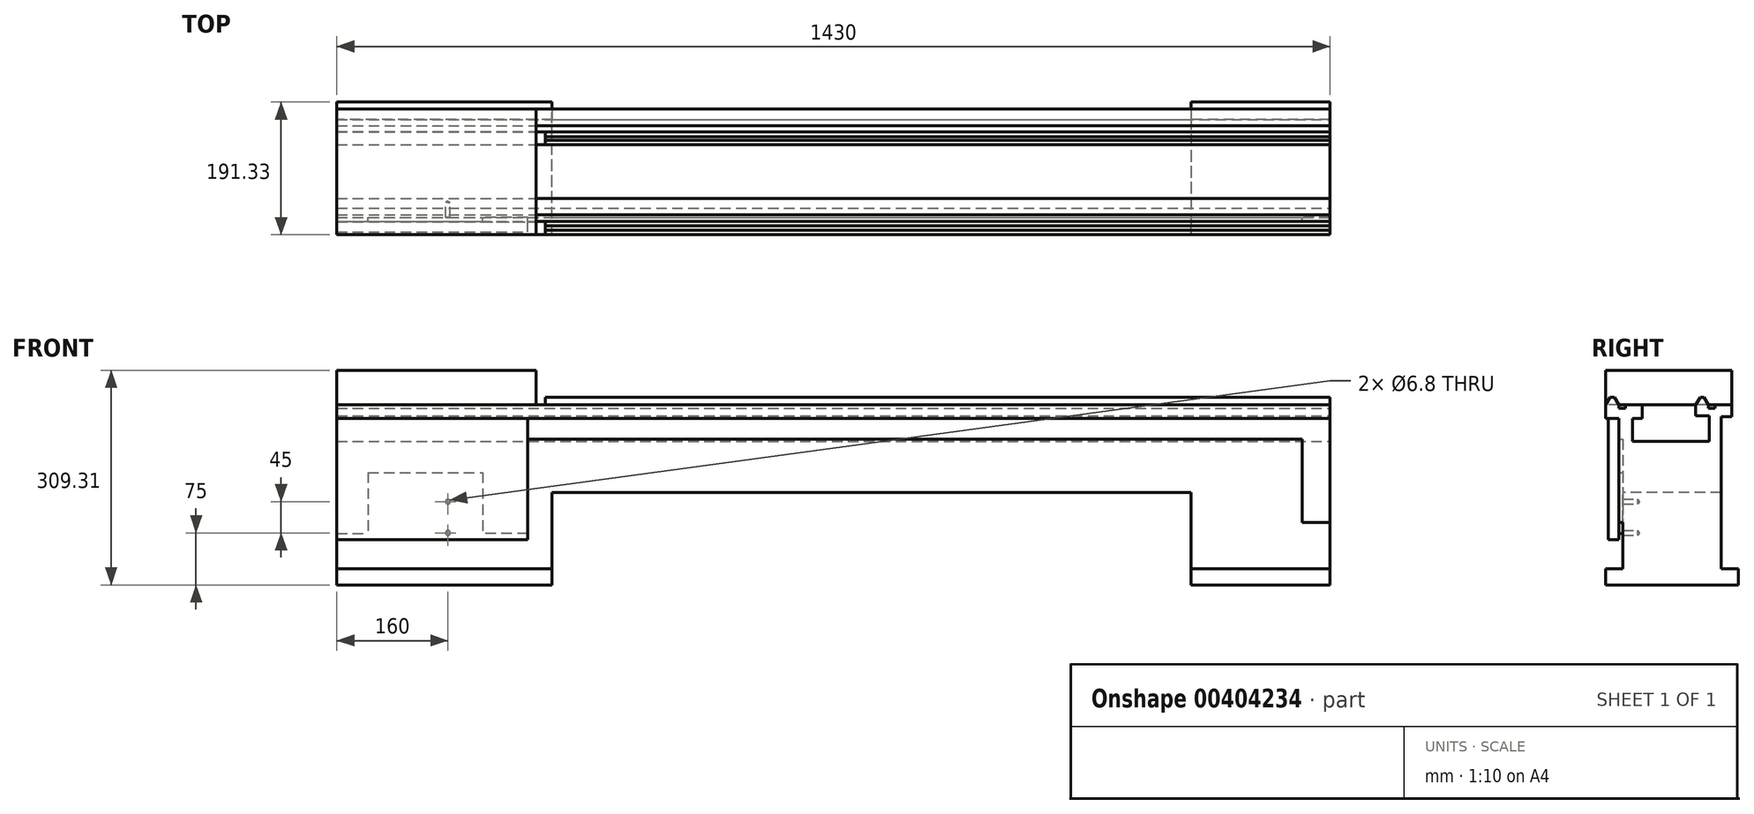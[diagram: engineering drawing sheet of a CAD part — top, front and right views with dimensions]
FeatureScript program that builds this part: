
annotation { "Feature Type Name" : "Feature", "Feature Type Description" : "" }
export const myFeature = defineFeature(function(context is Context, id is Id, definition is map)
    precondition{}
    {
        {
            var Q0;
            Q0=qCreatedBy(makeId("Right.planeOp"),FACE);
            var sketch = newSketch(context, id + "F0", { "sketchPlane" : qUnion([Q0])});
            skLineSegment(sketch, "E0", {"start": v(0, 19.31) * mm, "end": v(3.83, 25.95) * mm});
            skLineSegment(sketch, "E1", {"start": v(15.2, 25.95) * mm, "end": v(19.04, 19.31) * mm});
            skLineSegment(sketch, "E2", {"start": v(0, 19.31) * mm, "end": v(19.04, 19.31) * mm, "construction": true});
            skPoint(sketch, "E3.start.orphan", {"position": v(0, 0) * mm});
            skLineSegment(sketch, "E4", {"start": v(0, 0) * mm, "end": v(0, 19.31) * mm});
            skLineSegment(sketch, "E5", {"start": v(9.52, 25.95) * mm, "end": v(9.52, 19.31) * mm, "construction": true});
            skLineSegment(sketch, "E6", {"start": v(28.45, 19.31) * mm, "end": v(28.45, 14.51) * mm});
            skLineSegment(sketch, "E7", {"start": v(52.4, 19.31) * mm, "end": v(52.4, 0) * mm});
            skLineSegment(sketch, "E8", {"start": v(19.04, 19.31) * mm, "end": v(19.04, 14.51) * mm});
            skLineSegment(sketch, "E9", {"start": v(19.04, 14.51) * mm, "end": v(28.45, 14.51) * mm});
            skLineSegment(sketch, "E10", {"start": v(0, 0) * mm, "end": v(18.78, 0) * mm});
            skLineSegment(sketch, "E11", {"start": v(38.3, -32.97) * mm, "end": v(38.3, -32.97) * mm});
            skLineSegment(sketch, "E12", {"start": v(38.3, -32.97) * mm, "end": v(148.72, -32.97) * mm});
            skLineSegment(sketch, "E13", {"start": v(129.6, 19.31) * mm, "end": v(129.6, 3.67) * mm});
            skLineSegment(sketch, "E14.trimOffspring", {"start": v(28.45, 19.31) * mm, "end": v(52.4, 19.31) * mm});
            skLineSegment(sketch, "E15", {"start": v(136.07, 30.53) * mm, "end": v(141.32, 30.53) * mm});
            skLineSegment(sketch, "E16", {"start": v(129.6, 19.31) * mm, "end": v(136.07, 30.53) * mm});
            skLineSegment(sketch, "E17", {"start": v(141.32, 30.53) * mm, "end": v(147.8, 19.31) * mm});
            skLineSegment(sketch, "E18", {"start": v(181.37, 19.31) * mm, "end": v(181.37, 2.05) * mm});
            skLineSegment(sketch, "E19", {"start": v(147.8, 19.31) * mm, "end": v(147.8, 14.51) * mm});
            skLineSegment(sketch, "E20", {"start": v(147.8, 14.51) * mm, "end": v(157.11, 14.51) * mm});
            skLineSegment(sketch, "E21", {"start": v(157.11, 14.51) * mm, "end": v(157.11, 19.31) * mm});
            skLineSegment(sketch, "E22.trimOffspring", {"start": v(129.6, 19.31) * mm, "end": v(147.8, 19.31) * mm, "construction": true});
            skLineSegment(sketch, "E23", {"start": v(52.4, 0) * mm, "end": v(38.3, 0) * mm});
            skLineSegment(sketch, "E24", {"start": v(148.72, -32.97) * mm, "end": v(148.72, 3.67) * mm});
            skLineSegment(sketch, "E25", {"start": v(38.3, 0) * mm, "end": v(38.3, -32.97) * mm});
            skLineSegment(sketch, "E26", {"start": v(157.11, 19.31) * mm, "end": v(181.37, 19.31) * mm});
            skLineSegment(sketch, "E27", {"start": v(24.78, -106.67) * mm, "end": v(166.11, -106.67) * mm});
            skLineSegment(sketch, "E28", {"start": v(181.37, 2.05) * mm, "end": v(166.11, 2.05) * mm});
            skLineSegment(sketch, "E29", {"start": v(166.11, 2.05) * mm, "end": v(166.11, -106.67) * mm});
            skLineSegment(sketch, "E30", {"start": v(129.6, 3.67) * mm, "end": v(148.72, 3.67) * mm});
            skLineSegment(sketch, "E31", {"start": v(138.7, 30.53) * mm, "end": v(-64.68, 30.53) * mm, "construction": true});
            skLineSegment(sketch, "E32", {"start": v(3.83, 25.95) * mm, "end": v(6.48, 30.53) * mm});
            skLineSegment(sketch, "E33", {"start": v(15.2, 25.95) * mm, "end": v(12.56, 30.53) * mm});
            skLineSegment(sketch, "E34", {"start": v(12.56, 30.53) * mm, "end": v(6.48, 30.53) * mm});
            skLineSegment(sketch, "E35", {"start": v(24.78, -30) * mm, "end": v(24.78, -106.67) * mm});
            skLineSegment(sketch, "E36", {"start": v(24.78, -30) * mm, "end": v(18.78, -30) * mm});
            skLineSegment(sketch, "E37", {"start": v(18.78, -30) * mm, "end": v(18.78, 0) * mm});
            skSolve(sketch);
        }
        {
            var Q0;
            Q0=makeQuery(id+"F0.imprint","IMPRINT",FACE,{"disambiguationData":[TD([[makeQuery(id+"F0.imprint","IMPRINT",EDGE,{"derivedFrom":sQuery(id+"F0.wireOp",EDGE,"E0")}),-1.0]])]});
            extrude(context, id + "F1", {"entities" : qUnion([Q0]), "oppositeDirection" : true, "depth" : 1430 * mm, "offsetDistance" : 25 * mm});
        }
        {
            var Q0;
            Q0=makeQuery(id+"F1.opExtrude","SWEPT_FACE",FACE,{"disambiguationData":[OSD([sQuery(id+"F0.wireOp",EDGE,"E27")])]});
            var sketch = newSketch(context, id + "F2", { "sketchPlane" : qUnion([Q0])});
            skLineSegment(sketch, "E38.bottom", {"start": v(-1430, -24.78) * mm, "end": v(-1120, -24.78) * mm});
            skLineSegment(sketch, "E38.top", {"start": v(-1430, -166.11) * mm, "end": v(-1120, -166.11) * mm});
            skLineSegment(sketch, "E38.left", {"start": v(-1430, -24.78) * mm, "end": v(-1430, -166.11) * mm});
            skLineSegment(sketch, "E38.right", {"start": v(-1120, -24.78) * mm, "end": v(-1120, -166.11) * mm});
            skSolve(sketch);
        }
        {
            var Q0;
            Q0=makeQuery(id+"F2.imprint","IMPRINT",FACE,{"disambiguationData":[TD([[makeQuery(id+"F2.imprint","IMPRINT",EDGE,{"derivedFrom":sQuery(id+"F2.wireOp",EDGE,"E38.bottom")}),-1.0]])]});
            extrude(context, id + "F3", {"entities" : qUnion([Q0]), "operationType" : NewBodyOperationType.ADD, "depth" : 133.33 * mm, "offsetDistance" : 25 * mm});
        }
        {
            var Q0;
            Q0=makeQuery(id+"F1.opExtrude","SWEPT_FACE",FACE,{"disambiguationData":[OSD([sQuery(id+"F0.wireOp",EDGE,"E27")])]});
            var sketch = newSketch(context, id + "F4", { "sketchPlane" : qUnion([Q0])});
            skLineSegment(sketch, "E39.bottom", {"start": v(0, -166.11) * mm, "end": v(-200, -166.11) * mm});
            skLineSegment(sketch, "E39.top", {"start": v(0, -24.78) * mm, "end": v(-200, -24.78) * mm});
            skLineSegment(sketch, "E39.left", {"start": v(0, -166.11) * mm, "end": v(0, -24.78) * mm});
            skLineSegment(sketch, "E39.right", {"start": v(-200, -166.11) * mm, "end": v(-200, -24.78) * mm});
            skSolve(sketch);
        }
        {
            var Q0;
            Q0=makeQuery(id+"F4.imprint","IMPRINT",FACE,{"disambiguationData":[TD([[makeQuery(id+"F4.imprint","IMPRINT",EDGE,{"derivedFrom":sQuery(id+"F4.wireOp",EDGE,"E39.bottom")}),1.0]])]});
            extrude(context, id + "F5", {"entities" : qUnion([Q0]), "operationType" : NewBodyOperationType.ADD, "depth" : 133.33 * mm, "offsetDistance" : 25 * mm});
        }
        {
            var Q0;
            Q0=makeQuery(id+"F5.boolean.opBoolean","MERGE",FACE,{"derivedFrom":[makeQuery(id+"F3.boolean.opBoolean","MERGE",FACE,{"derivedFrom":[makeQuery(id+"F1.opExtrude","SWEPT_FACE",FACE,{"disambiguationData":[OSD([sQuery(id+"F0.wireOp",EDGE,"E35")])]}),makeQuery(id+"F3.opExtrude","SWEPT_FACE",FACE,{"disambiguationData":[OSD([sQuery(id+"F2.wireOp",EDGE,"E38.bottom")])]})]}),makeQuery(id+"F5.opExtrude","SWEPT_FACE",FACE,{"disambiguationData":[OSD([sQuery(id+"F4.wireOp",EDGE,"E39.top")])]})]});
            var sketch = newSketch(context, id + "F6", { "sketchPlane" : qUnion([Q0])});
            skLineSegment(sketch, "E40", {"start": v(-1270, -115.03) * mm, "end": v(-1270, -199.05) * mm, "construction": true});
            skLineSegment(sketch, "E41", {"start": v(-1270, -199.05) * mm, "end": v(-1270, -115.03) * mm, "construction": true});
            skPoint(sketch, "E42", {"position": v(-1270, -120) * mm});
            skPoint(sketch, "E43", {"position": v(-1270, -165) * mm});
            skSolve(sketch);
        }
        {
            var Q0;
            Q0=sQuery(id+"F6.wireOp",VERTEX,"E42");
            var Q1;
            Q1=sQuery(id+"F6.wireOp",VERTEX,"E43");
            var Q2;
            Q2=makeQuery(id+"F1.opExtrude","SWEPT_BODY",BODY,{"disambiguationData":[OSD([sQuery(id+"F0.wireOp",EDGE,"E0"),sQuery(id+"F0.wireOp",EDGE,"E1"),sQuery(id+"F0.wireOp",EDGE,"E4"),sQuery(id+"F0.wireOp",EDGE,"E6"),sQuery(id+"F0.wireOp",EDGE,"E7"),sQuery(id+"F0.wireOp",EDGE,"E8"),sQuery(id+"F0.wireOp",EDGE,"E9"),sQuery(id+"F0.wireOp",EDGE,"E10"),sQuery(id+"F0.wireOp",EDGE,"YCXMaznk-yFnF-7irV-mpq2-gFufozlePJW7"),sQuery(id+"F0.wireOp",EDGE,"E12"),sQuery(id+"F0.wireOp",EDGE,"E13"),sQuery(id+"F0.wireOp",EDGE,"E14.trimOffspring"),sQuery(id+"F0.wireOp",EDGE,"E15"),sQuery(id+"F0.wireOp",EDGE,"E16"),sQuery(id+"F0.wireOp",EDGE,"E17"),sQuery(id+"F0.wireOp",EDGE,"E18"),sQuery(id+"F0.wireOp",EDGE,"E19"),sQuery(id+"F0.wireOp",EDGE,"E20"),sQuery(id+"F0.wireOp",EDGE,"E21"),sQuery(id+"F0.wireOp",EDGE,"E23"),sQuery(id+"F0.wireOp",EDGE,"E24"),sQuery(id+"F0.wireOp",EDGE,"E25"),sQuery(id+"F0.wireOp",EDGE,"E26"),sQuery(id+"F0.wireOp",EDGE,"E27"),sQuery(id+"F0.wireOp",EDGE,"E28"),sQuery(id+"F0.wireOp",EDGE,"E29"),sQuery(id+"F0.wireOp",EDGE,"E30"),sQuery(id+"F0.wireOp",EDGE,"E32"),sQuery(id+"F0.wireOp",EDGE,"E33"),sQuery(id+"F0.wireOp",EDGE,"E34"),sQuery(id+"F0.wireOp",EDGE,"nFRyOStG-R2Nf-dePJ-d9Yt-8JFO99bLOjxj"),sQuery(id+"F0.wireOp",EDGE,"E35")])]});
            hole(context, id + "F7", {"style" : HoleStyle.SIMPLE, "endStyle" : HoleEndStyle.BLIND, "standardTappedOrClearance" : lookupTablePath({ "standard" : "ISO", "engagement" : "75%", "pitch" : "1.25 mm", "size" : "M8", "type" : "Tapped" }), "standardBlindInLast" : lookupTablePath({ "standard" : "ISO", "engagement" : "75%", "pitch" : "1.25 mm", "size" : "M8", "type" : "Tapped" }), "holeDiameter" : 6.8 * mm, "majorDiameter" : 8 * mm, "showTappedDepth" : true, "holeDepth" : 21.65 * mm, "isTappedThrough" : true, "tappedDepth" : 17.9 * mm, "tapClearance" : 3, "startFromSketch" : true, "locations" : qUnion([Q0, Q1]), "scope" : qUnion([Q2])});
        }
        {
            var Q0;
            {var subQ0=sQuery(id+"F2.wireOp",EDGE,"E38.bottom");Q0=makeQuery(id+"F6.imprint","IMPRINT",FACE,{"disambiguationData":[TD([[makeQuery(id+"F6.imprint","IMPRINT",EDGE,{"derivedFrom":makeQuery(id+"F3.opExtrude","CAP_EDGE",EDGE,{"disambiguationData":[OSD([subQ0])],"isStart":false})}),1.0]])]});}
            var sketch = newSketch(context, id + "F8", { "sketchPlane" : qUnion([Q0])});
            skLineSegment(sketch, "E44.bottom", {"start": v(-1430, -30) * mm, "end": v(-1155, -30) * mm});
            skLineSegment(sketch, "E44.top", {"start": v(-1385, -78) * mm, "end": v(-1220, -78) * mm});
            skLineSegment(sketch, "E45.top", {"start": v(-1430, -166) * mm, "end": v(-1385, -166) * mm});
            skLineSegment(sketch, "E45.right", {"start": v(-1385, -78) * mm, "end": v(-1385, -166) * mm});
            skLineSegment(sketch, "E46.top", {"start": v(-1155, -166) * mm, "end": v(-1220, -166) * mm});
            skLineSegment(sketch, "E46.right", {"start": v(-1220, -78) * mm, "end": v(-1220, -166) * mm});
            skLineSegment(sketch, "E47", {"start": v(-1430, -30) * mm, "end": v(-1430, -166) * mm});
            skLineSegment(sketch, "E48", {"start": v(-1155, -30) * mm, "end": v(-1155, -166) * mm});
            skSolve(sketch);
        }
        {
            var Q0;
            Q0=makeQuery(id+"F8.imprint","IMPRINT",FACE,{"disambiguationData":[TD([[makeQuery(id+"F8.imprint","IMPRINT",EDGE,{"derivedFrom":sQuery(id+"F8.wireOp",EDGE,"E44.bottom")}),-1.0]])]});
            var Q1;
            Q1=makeQuery(id+"F21.boolean.opBoolean","MERGE",FACE,{"derivedFrom":[makeQuery(id+"F1.opExtrude","SWEPT_FACE",FACE,{"disambiguationData":[OSD([sQuery(id+"F0.wireOp",EDGE,"E37")])]}),makeQuery(id+"F21.opExtrude","CAP_FACE",FACE,{"disambiguationData":[OSD([sQuery(id+"F20.wireOp",EDGE,"E54.bottom"),sQuery(id+"F20.wireOp",EDGE,"E54.top"),sQuery(id+"F20.wireOp",EDGE,"E54.left"),sQuery(id+"F20.wireOp",EDGE,"E54.right")])],"isStart":false})]});
            extrude(context, id + "F9", {"entities" : qUnion([Q0]), "operationType" : NewBodyOperationType.ADD, "endBound" : BoundingType.UP_TO_SURFACE, "depth" : 25 * mm, "endBoundEntityFace" : qUnion([Q1]), "offsetDistance" : 25 * mm});
        }
        {
            var Q0;
            Q0=makeQuery(id+"F9.boolean.opBoolean","MERGE",FACE,{"derivedFrom":[makeQuery(id+"F1.opExtrude","SWEPT_FACE",FACE,{"disambiguationData":[OSD([sQuery(id+"F0.wireOp",EDGE,"E37")])]}),makeQuery(id+"F9.opExtrude","CAP_FACE",FACE,{"disambiguationData":[OSD([sQuery(id+"F8.wireOp",EDGE,"E44.bottom"),sQuery(id+"F8.wireOp",EDGE,"E44.top"),sQuery(id+"F8.wireOp",EDGE,"E45.top"),sQuery(id+"F8.wireOp",EDGE,"E45.right"),sQuery(id+"F8.wireOp",EDGE,"E46.top"),sQuery(id+"F8.wireOp",EDGE,"E46.right"),sQuery(id+"F8.wireOp",EDGE,"E47"),sQuery(id+"F8.wireOp",EDGE,"E48")])],"isStart":false})]});
            var sketch = newSketch(context, id + "F10", { "sketchPlane" : qUnion([Q0])});
            skLineSegment(sketch, "E49.bottom", {"start": v(-1430, 0) * mm, "end": v(-1155, 0) * mm});
            skLineSegment(sketch, "E49.top", {"start": v(-1430, -175) * mm, "end": v(-1155, -175) * mm});
            skLineSegment(sketch, "E49.left", {"start": v(-1430, 0) * mm, "end": v(-1430, -175) * mm});
            skLineSegment(sketch, "E49.right", {"start": v(-1155, 0) * mm, "end": v(-1155, -175) * mm});
            skSolve(sketch);
        }
        {
            var Q0;
            {var subQ1=sQuery(id+"F10.wireOp",EDGE,"E49.bottom");Q0=makeQuery(id+"F10.imprint","IMPRINT",FACE,{"disambiguationData":[TD([[makeQuery(id+"F10.imprint","IMPRINT",EDGE,{"derivedFrom":subQ1}),-1.0]])]});}
            var Q1;
            {var subQ0=sQuery(id+"F10.wireOp",EDGE,"E49.right");var subQ1=sQuery(id+"F10.wireOp",EDGE,"E49.top");var subQ2=makeQuery(id+"F10.imprint","INTERSECT",VERTEX,{"derivedFrom":[subQ1,subQ0]});Q1=makeQuery(id+"F10.imprint","IMPRINT",FACE,{"disambiguationData":[TD([[makeQuery(id+"F10.imprint","IMPRINT",EDGE,{"disambiguationData":[TD([[subQ2,1.0]])],"derivedFrom":subQ0}),-1.0]])]});}
            extrude(context, id + "F11", {"entities" : qUnion([Q0, Q1]), "depth" : 15 * mm, "offsetDistance" : 25 * mm});
        }
        {
            var Q0;
            {var subQ0=sQuery(id+"F2.wireOp",EDGE,"E38.bottom");Q0=makeQuery(id+"F6.imprint","IMPRINT",FACE,{"disambiguationData":[TD([[makeQuery(id+"F6.imprint","IMPRINT",EDGE,{"derivedFrom":makeQuery(id+"F3.opExtrude","CAP_EDGE",EDGE,{"disambiguationData":[OSD([subQ0])],"isStart":false})}),1.0]])]});}
            var sketch = newSketch(context, id + "F12", { "sketchPlane" : qUnion([Q0])});
            skLineSegment(sketch, "E50.bottom", {"start": v(-1430, -240) * mm, "end": v(-1120, -240) * mm});
            skLineSegment(sketch, "E50.top", {"start": v(-1430, -217) * mm, "end": v(-1120, -217) * mm});
            skLineSegment(sketch, "E50.left", {"start": v(-1430, -240) * mm, "end": v(-1430, -217) * mm});
            skLineSegment(sketch, "E50.right", {"start": v(-1120, -240) * mm, "end": v(-1120, -217) * mm});
            skSolve(sketch);
        }
        {
            var Q0;
            Q0 = qSketchRegion(id + "F12", true);
            extrude(context, id + "F13", {"entities" : qUnion([Q0]), "operationType" : NewBodyOperationType.ADD, "depth" : 25 * mm, "offsetDistance" : 25 * mm});
        }
        {
            var Q0;
            Q0=makeQuery(id+"F5.boolean.opBoolean","MERGE",FACE,{"derivedFrom":[makeQuery(id+"F3.boolean.opBoolean","MERGE",FACE,{"derivedFrom":[makeQuery(id+"F1.opExtrude","SWEPT_FACE",FACE,{"disambiguationData":[OSD([sQuery(id+"F0.wireOp",EDGE,"E29")])]}),makeQuery(id+"F3.opExtrude","SWEPT_FACE",FACE,{"disambiguationData":[OSD([sQuery(id+"F2.wireOp",EDGE,"E38.top")])]})]}),makeQuery(id+"F5.opExtrude","SWEPT_FACE",FACE,{"disambiguationData":[OSD([sQuery(id+"F4.wireOp",EDGE,"E39.bottom")])]})]});
            var sketch = newSketch(context, id + "F14", { "sketchPlane" : qUnion([Q0])});
            skLineSegment(sketch, "E51.bottom", {"start": v(1120, -240) * mm, "end": v(1430, -240) * mm});
            skLineSegment(sketch, "E51.top", {"start": v(1120, -217) * mm, "end": v(1430, -217) * mm});
            skLineSegment(sketch, "E51.left", {"start": v(1120, -240) * mm, "end": v(1120, -217) * mm});
            skLineSegment(sketch, "E51.right", {"start": v(1430, -240) * mm, "end": v(1430, -217) * mm});
            skSolve(sketch);
        }
        {
            var Q0;
            Q0=makeQuery(id+"F14.imprint","IMPRINT",FACE,{"disambiguationData":[TD([[makeQuery(id+"F14.imprint","IMPRINT",EDGE,{"derivedFrom":sQuery(id+"F14.wireOp",EDGE,"E51.bottom")}),-1.0]])]});
            extrude(context, id + "F15", {"entities" : qUnion([Q0]), "operationType" : NewBodyOperationType.ADD, "depth" : 25 * mm, "offsetDistance" : 25 * mm});
        }
        {
            var Q0;
            {var subQ0=sQuery(id+"F2.wireOp",EDGE,"E38.bottom");Q0=makeQuery(id+"F6.imprint","IMPRINT",FACE,{"disambiguationData":[TD([[makeQuery(id+"F6.imprint","IMPRINT",EDGE,{"derivedFrom":makeQuery(id+"F3.opExtrude","CAP_EDGE",EDGE,{"disambiguationData":[OSD([subQ0])],"isStart":false})}),1.0]])]});}
            var sketch = newSketch(context, id + "F16", { "sketchPlane" : qUnion([Q0])});
            skLineSegment(sketch, "E52.bottom", {"start": v(-200, -217) * mm, "end": v(0, -217) * mm});
            skLineSegment(sketch, "E52.top", {"start": v(-200, -240) * mm, "end": v(0, -240) * mm});
            skLineSegment(sketch, "E52.left", {"start": v(-200, -217) * mm, "end": v(-200, -240) * mm});
            skLineSegment(sketch, "E52.right", {"start": v(0, -217) * mm, "end": v(0, -240) * mm});
            skSolve(sketch);
        }
        {
            var Q0;
            Q0 = qSketchRegion(id + "F16", true);
            extrude(context, id + "F17", {"entities" : qUnion([Q0]), "operationType" : NewBodyOperationType.ADD, "depth" : 25 * mm, "offsetDistance" : 25 * mm});
        }
        {
            var Q0;
            Q0=makeQuery(id+"F5.boolean.opBoolean","MERGE",FACE,{"derivedFrom":[makeQuery(id+"F3.boolean.opBoolean","MERGE",FACE,{"derivedFrom":[makeQuery(id+"F1.opExtrude","SWEPT_FACE",FACE,{"disambiguationData":[OSD([sQuery(id+"F0.wireOp",EDGE,"E29")])]}),makeQuery(id+"F3.opExtrude","SWEPT_FACE",FACE,{"disambiguationData":[OSD([sQuery(id+"F2.wireOp",EDGE,"E38.top")])]})]}),makeQuery(id+"F5.opExtrude","SWEPT_FACE",FACE,{"disambiguationData":[OSD([sQuery(id+"F4.wireOp",EDGE,"E39.bottom")])]})]});
            var sketch = newSketch(context, id + "F18", { "sketchPlane" : qUnion([Q0])});
            skLineSegment(sketch, "E53.bottom", {"start": v(0, -240) * mm, "end": v(200, -240) * mm});
            skLineSegment(sketch, "E53.top", {"start": v(0, -217) * mm, "end": v(200, -217) * mm});
            skLineSegment(sketch, "E53.left", {"start": v(0, -240) * mm, "end": v(0, -217) * mm});
            skLineSegment(sketch, "E53.right", {"start": v(200, -240) * mm, "end": v(200, -217) * mm});
            skSolve(sketch);
        }
        {
            var Q0;
            Q0 = qSketchRegion(id + "F18", true);
            extrude(context, id + "F19", {"entities" : qUnion([Q0]), "operationType" : NewBodyOperationType.ADD, "depth" : 25 * mm, "offsetDistance" : 25 * mm});
        }
        {
            var Q0;
            {var subQ0=sQuery(id+"F2.wireOp",EDGE,"E38.bottom");Q0=makeQuery(id+"F6.imprint","IMPRINT",FACE,{"disambiguationData":[TD([[makeQuery(id+"F6.imprint","IMPRINT",EDGE,{"derivedFrom":makeQuery(id+"F3.opExtrude","CAP_EDGE",EDGE,{"disambiguationData":[OSD([subQ0])],"isStart":false})}),1.0]])]});}
            var sketch = newSketch(context, id + "F20", { "sketchPlane" : qUnion([Q0])});
            skLineSegment(sketch, "E54.bottom", {"start": v(0, -30) * mm, "end": v(-40, -30) * mm});
            skLineSegment(sketch, "E54.top", {"start": v(0, -150) * mm, "end": v(-40, -150) * mm});
            skLineSegment(sketch, "E54.left", {"start": v(0, -30) * mm, "end": v(0, -150) * mm});
            skLineSegment(sketch, "E54.right", {"start": v(-40, -30) * mm, "end": v(-40, -150) * mm});
            skSolve(sketch);
        }
        {
            var Q0;
            Q0 = qSketchRegion(id + "F20", true);
            var Q1;
            Q1=makeQuery(id+"F1.opExtrude","SWEPT_FACE",FACE,{"disambiguationData":[OSD([sQuery(id+"F0.wireOp",EDGE,"E37")])]});
            extrude(context, id + "F21", {"entities" : qUnion([Q0]), "operationType" : NewBodyOperationType.ADD, "endBound" : BoundingType.UP_TO_SURFACE, "depth" : 25 * mm, "endBoundEntityFace" : qUnion([Q1]), "offsetDistance" : 25 * mm});
        }
        {
            var Q0;
            Q0=makeQuery(id+"F15.boolean.opBoolean","MERGE",FACE,{"derivedFrom":[makeQuery(id+"F13.boolean.opBoolean","MERGE",FACE,{"derivedFrom":[makeQuery(id+"F9.boolean.opBoolean","MERGE",FACE,{"derivedFrom":[makeQuery(id+"F3.boolean.opBoolean","MERGE",FACE,{"derivedFrom":[makeQuery(id+"F1.opExtrude","CAP_FACE",FACE,{"disambiguationData":[OSD([sQuery(id+"F0.wireOp",EDGE,"E0"),sQuery(id+"F0.wireOp",EDGE,"E1"),sQuery(id+"F0.wireOp",EDGE,"E4"),sQuery(id+"F0.wireOp",EDGE,"E6"),sQuery(id+"F0.wireOp",EDGE,"E7"),sQuery(id+"F0.wireOp",EDGE,"E8"),sQuery(id+"F0.wireOp",EDGE,"E9"),sQuery(id+"F0.wireOp",EDGE,"E10"),sQuery(id+"F0.wireOp",EDGE,"E12"),sQuery(id+"F0.wireOp",EDGE,"E13"),sQuery(id+"F0.wireOp",EDGE,"E14.trimOffspring"),sQuery(id+"F0.wireOp",EDGE,"E15"),sQuery(id+"F0.wireOp",EDGE,"E16"),sQuery(id+"F0.wireOp",EDGE,"E17"),sQuery(id+"F0.wireOp",EDGE,"E18"),sQuery(id+"F0.wireOp",EDGE,"E19"),sQuery(id+"F0.wireOp",EDGE,"E20"),sQuery(id+"F0.wireOp",EDGE,"E21"),sQuery(id+"F0.wireOp",EDGE,"E23"),sQuery(id+"F0.wireOp",EDGE,"E24"),sQuery(id+"F0.wireOp",EDGE,"E25"),sQuery(id+"F0.wireOp",EDGE,"E26"),sQuery(id+"F0.wireOp",EDGE,"E27"),sQuery(id+"F0.wireOp",EDGE,"E28"),sQuery(id+"F0.wireOp",EDGE,"E29"),sQuery(id+"F0.wireOp",EDGE,"E30"),sQuery(id+"F0.wireOp",EDGE,"E32"),sQuery(id+"F0.wireOp",EDGE,"E33"),sQuery(id+"F0.wireOp",EDGE,"E34"),sQuery(id+"F0.wireOp",EDGE,"E35"),sQuery(id+"F0.wireOp",EDGE,"E36"),sQuery(id+"F0.wireOp",EDGE,"E37")])],"isStart":false}),makeQuery(id+"F3.opExtrude","SWEPT_FACE",FACE,{"disambiguationData":[OSD([sQuery(id+"F2.wireOp",EDGE,"E38.left")])]})]}),makeQuery(id+"F9.opExtrude","SWEPT_FACE",FACE,{"disambiguationData":[OSD([sQuery(id+"F8.wireOp",EDGE,"E47")])]})]}),makeQuery(id+"F13.opExtrude","SWEPT_FACE",FACE,{"disambiguationData":[OSD([sQuery(id+"F12.wireOp",EDGE,"E50.left")])]})]}),makeQuery(id+"F15.opExtrude","SWEPT_FACE",FACE,{"disambiguationData":[OSD([sQuery(id+"F14.wireOp",EDGE,"E51.right")])]})]});
            var sketch = newSketch(context, id + "F22", { "sketchPlane" : qUnion([Q0])});
            skLineSegment(sketch, "E55", {"start": v(-147.8, 19.31) * mm, "end": v(-129.6, 19.31) * mm});
            skLineSegment(sketch, "E56", {"start": v(-147.8, 19.31) * mm, "end": v(-141.32, 30.53) * mm});
            skLineSegment(sketch, "E57", {"start": v(-141.32, 30.53) * mm, "end": v(-136.07, 30.53) * mm});
            skLineSegment(sketch, "E58", {"start": v(-136.07, 30.53) * mm, "end": v(-129.6, 19.31) * mm});
            skLineSegment(sketch, "E59", {"start": v(-19.04, 19.31) * mm, "end": v(-12.56, 30.53) * mm});
            skLineSegment(sketch, "E60", {"start": v(-12.56, 30.53) * mm, "end": v(-6.48, 30.53) * mm});
            skLineSegment(sketch, "E61", {"start": v(-6.48, 30.53) * mm, "end": v(0, 19.31) * mm});
            skLineSegment(sketch, "E62.trimOffspring", {"start": v(-19.04, 19.31) * mm, "end": v(0, 19.31) * mm});
            skSolve(sketch);
        }
        {
            var Q0;
            Q0=makeQuery(id+"F22.imprint","IMPRINT",FACE,{"disambiguationData":[TD([[makeQuery(id+"F22.imprint","IMPRINT",EDGE,{"derivedFrom":sQuery(id+"F22.wireOp",EDGE,"E55")}),1.0]])]});
            var Q1;
            Q1=makeQuery(id+"F22.imprint","IMPRINT",FACE,{"disambiguationData":[TD([[makeQuery(id+"F22.imprint","IMPRINT",EDGE,{"derivedFrom":sQuery(id+"F22.wireOp",EDGE,"E59")}),1.0]])]});
            extrude(context, id + "F23", {"entities" : qUnion([Q0, Q1]), "operationType" : NewBodyOperationType.REMOVE, "oppositeDirection" : true, "depth" : 300 * mm, "offsetDistance" : 25 * mm});
        }
        {
            var Q0;
            Q0=makeQuery(id+"F1.opExtrude","SWEPT_FACE",FACE,{"disambiguationData":[OSD([sQuery(id+"F0.wireOp",EDGE,"E26")])]});
            var sketch = newSketch(context, id + "F24", { "sketchPlane" : qUnion([Q0])});
            skLineSegment(sketch, "E63.bottom", {"start": v(-1430, 181.37) * mm, "end": v(-1143.23, 181.37) * mm});
            skLineSegment(sketch, "E63.top", {"start": v(-1430, 0) * mm, "end": v(-1143.23, 0) * mm});
            skLineSegment(sketch, "E63.left", {"start": v(-1430, 181.37) * mm, "end": v(-1430, 0) * mm});
            skLineSegment(sketch, "E63.right", {"start": v(-1143.23, 181.37) * mm, "end": v(-1143.23, 0) * mm});
            skSolve(sketch);
        }
        {
            var Q0;
            {var subQ0=sQuery(id+"F24.wireOp",EDGE,"E63.top");Q0=makeQuery(id+"F24.imprint","IMPRINT",FACE,{"disambiguationData":[TD([[makeQuery(id+"F24.imprint","IMPRINT",EDGE,{"derivedFrom":subQ0}),1.0]])]});}
            var Q1;
            {var subQ0=sQuery(id+"F24.wireOp",EDGE,"E63.bottom");Q1=makeQuery(id+"F24.imprint","IMPRINT",FACE,{"disambiguationData":[TD([[makeQuery(id+"F24.imprint","IMPRINT",EDGE,{"derivedFrom":subQ0}),-1.0]])]});}
            extrude(context, id + "F25", {"entities" : qUnion([Q0, Q1]), "depth" : 50 * mm, "offsetDistance" : 25 * mm});
        }
    });
